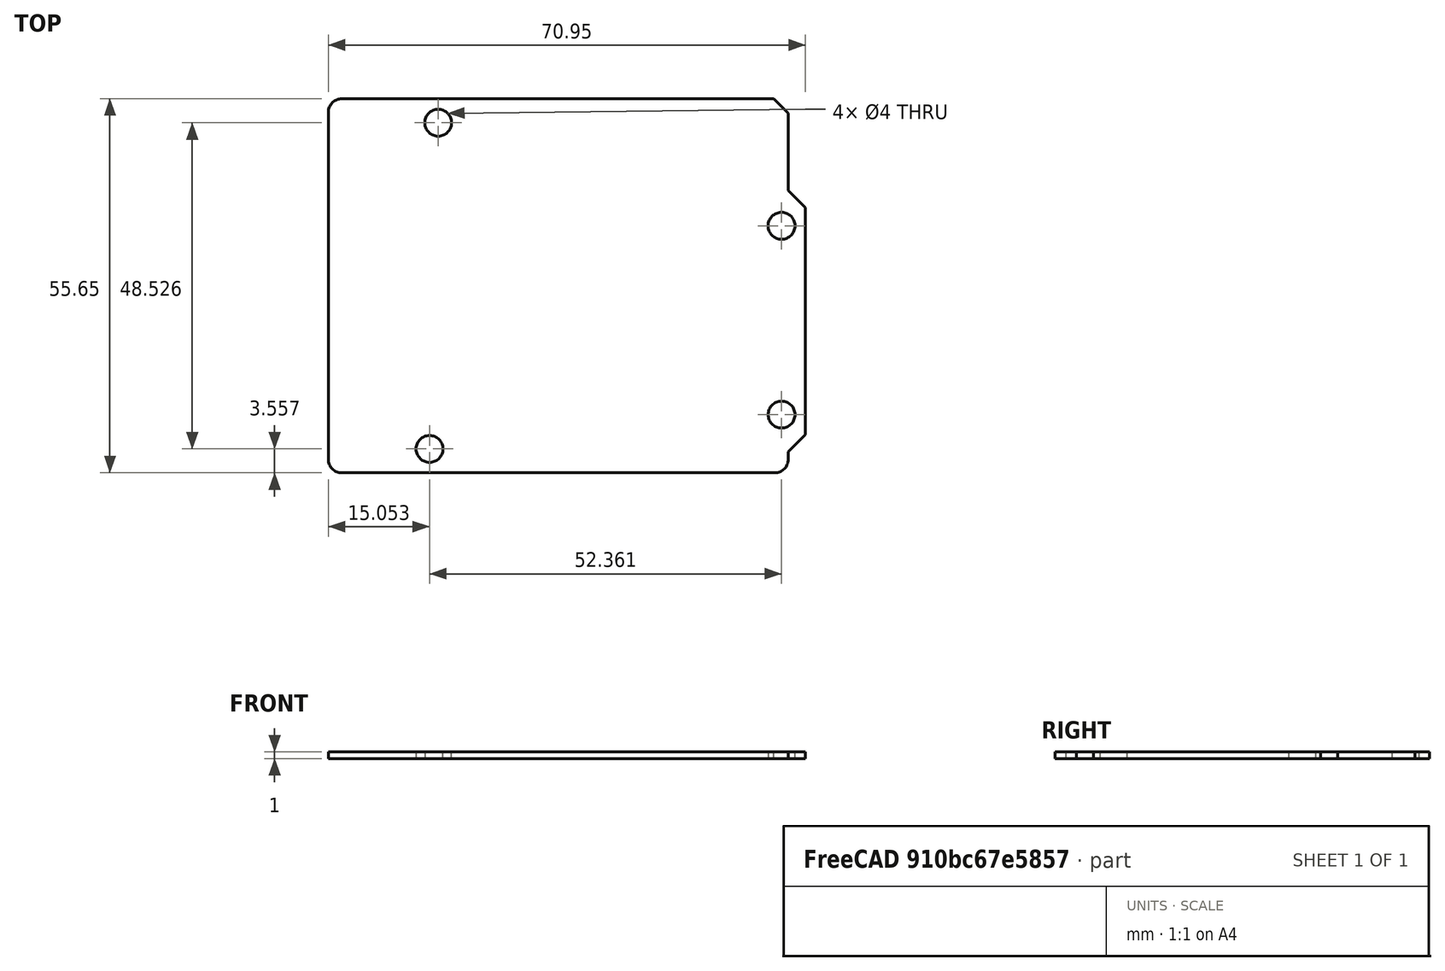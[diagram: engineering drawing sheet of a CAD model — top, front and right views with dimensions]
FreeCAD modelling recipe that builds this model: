
FCSTD DOCUMENT  (FreeCAD 0.19R)
Label: CAIXA-ARDUINO_01
License: Creative Commons Attribution-NonCommercial-ShareAlike
LicenseURL: http://creativecommons.org/licenses/by-nc-sa/4.0/
objects: Part::Feature×1, Sketcher::SketchObject×1, Part::Extrusion×1
note: 3 computed .brp shape members not serialized (recipe doc carries the construction recipe); baked Part::Feature solids carry a one-line shape summary decoded from their .brp

FEATURE [Part::Feature] ARDUINO_3D_SCALED
  Placement = pos=(-1,-1,0) rot=(0,0,1;0rad)
  shape: bbox 75.35 x 53.65 x 13.2 mm, 104 faces, 0 solids (baked)
FEATURE [Sketcher::SketchObject] Sketch
  ExternalGeometry = -> [ARDUINO_3D_SCALED]
  sketch-geometry (25):
    g0: LineSegment StartX=1 StartY=54.65 StartZ=0 EndX=65.2642 EndY=54.65 EndZ=0
    g1: LineSegment StartX=65.2642 StartY=54.65 StartZ=0 EndX=67.4 EndY=52.5142 EndZ=0
    g2: LineSegment StartX=67.4 StartY=52.5142 StartZ=0 EndX=67.4 EndY=41.0142 EndZ=0
    g3: LineSegment StartX=67.4 StartY=41.0142 StartZ=0 EndX=69.95 EndY=38.4642 EndZ=0
    g4: LineSegment StartX=69.95 StartY=38.4642 StartZ=0 EndX=69.95 EndY=4.68579 EndZ=0
    g5: LineSegment StartX=69.95 StartY=4.68579 StartZ=0 EndX=67.4 EndY=2.13579 EndZ=0
    g6: LineSegment StartX=67.4 StartY=2.13579 StartZ=0 EndX=67.4 EndY=1 EndZ=0
    g7: LineSegment StartX=65.4 StartY=-1 StartZ=0 EndX=1 EndY=-1 EndZ=0
    g8: LineSegment StartX=-1 StartY=1 StartZ=0 EndX=-1 EndY=52.65 EndZ=0
    g9: ArcOfCircle CenterX=1 CenterY=52.65 CenterZ=0 NormalX=0 NormalY=0 NormalZ=1 AngleXU=0 Radius=2 StartAngle=1.5708 EndAngle=3.14159
    g10: ArcOfCircle CenterX=1 CenterY=1 CenterZ=0 NormalX=0 NormalY=0 NormalZ=1 AngleXU=0 Radius=2 StartAngle=3.14159 EndAngle=4.71239
    g11: ArcOfCircle CenterX=65.4 CenterY=1 CenterZ=0 NormalX=0 NormalY=0 NormalZ=1 AngleXU=0 Radius=2 StartAngle=4.71239 EndAngle=6.28319
    g12: LineSegment [constr] StartX=67.675 StartY=39.325 StartZ=0 EndX=68.3821 EndY=40.0321 EndZ=0
    g13: LineSegment [constr] StartX=66.4 StartY=46.35 StartZ=0 EndX=67.4 EndY=46.35 EndZ=0
    g14: LineSegment [constr] StartX=65.625 StartY=52.875 StartZ=0 EndX=66.3321 EndY=53.5821 EndZ=0
    g15: LineSegment [constr] StartX=32.925 StartY=53.65 StartZ=0 EndX=32.925 EndY=54.65 EndZ=0
    g16: LineSegment [constr] StartX=4e-16 StartY=26.825 StartZ=0 EndX=-1 EndY=26.825 EndZ=0
    g17: LineSegment [constr] StartX=39.1673 StartY=1e-16 StartZ=0 EndX=39.1673 EndY=-1 EndZ=0
    g18: LineSegment [constr] StartX=66.4 StartY=1.56789 StartZ=0 EndX=67.4 EndY=1.56789 EndZ=0
    g19: LineSegment [constr] StartX=67.675 StartY=3.825 StartZ=0 EndX=68.3821 EndY=3.11789 EndZ=0
    g20: LineSegment [constr] StartX=68.95 StartY=21.575 StartZ=0 EndX=69.95 EndY=21.575 EndZ=0
    g21: Circle CenterX=15.3341 CenterY=51.0829 CenterZ=0 NormalX=0 NormalY=0 NormalZ=1 AngleXU=0 Radius=2
    g22: Circle CenterX=66.41 CenterY=35.7498 CenterZ=0 NormalX=0 NormalY=0 NormalZ=1 AngleXU=0 Radius=2
    g23: Circle CenterX=66.4139 CenterY=7.6684 CenterZ=0 NormalX=0 NormalY=0 NormalZ=1 AngleXU=0 Radius=2
    g24: Circle CenterX=14.0525 CenterY=2.55698 CenterZ=0 NormalX=0 NormalY=0 NormalZ=1 AngleXU=0 Radius=2
  constraints (65):
    c: Horizontal(g0)
    c: Coincident(g0,g1)
    c: Coincident(g1,g2)
    c: Vertical(g2)
    c: Coincident(g2,g3)
    c: Coincident(g3,g4)
    c: Coincident(g4,g5)
    c: Coincident(g5,g6)
    c: Vertical(g6)
    c: Horizontal(g7)
    c: Vertical(g8)
    c: Vertical(g4)
    c: Tangent(g0,g9) = 1.5708
    c: Tangent(g8,g9) = 1.5708
    c: Tangent(g7,g10) = 1.5708
    c: Tangent(g8,g10) = 1.5708
    c: Tangent(g6,g11) = 1.5708
    c: Tangent(g7,g11) = 1.5708
    c: Coincident(g11,g-6)
    c: Coincident(g10,g-4)
    c: Coincident(g9,g-14)
    c: Parallel(g3,g-10)
    c: Parallel(g-12,g1)
    c: Parallel(g5,g-8)
    c: PointOnObject(g12,g3)
    c: PointOnObject(g13,g2)
    c: Horizontal(g13)
    c: PointOnObject(g14,g1)
    c: Vertical(g15)
    c: PointOnObject(g16,g8)
    c: PointOnObject(g17,g-3)
    c: PointOnObject(g17,g7)
    c: Horizontal(g18)
    c: PointOnObject(g19,g5)
    c: PointOnObject(g20,g4)
    c: Horizontal(g20)
    c: Symmetric(g-9,g-9,g20)
    c: Symmetric(g-10,g-10,g12)
    c: Symmetric(g-11,g-11,g13)
    c: Perpendicular(g12,g-10)
    c: Symmetric(g-12,g-12,g14)
    c: Perpendicular(g-12,g14)
    c: Symmetric(g-13,g-13,g15)
    c: Symmetric(g-5,g-5,g16)
    c: Horizontal(g16)
    c: Symmetric(g-8,g-8,g19)
    c: Perpendicular(g-8,g19)
    c: Equal(g20,g12)
    c: Equal(g12,g13)
    c: Equal(g13,g14)
    c: Equal(g14,g15)
    c: Equal(g15,g16)
    c: Equal(g16,g17)
    c: Equal(g17,g18)
    c: Equal(g18,g19)
    c: Symmetric(g6,g6,g18)
    c: DistanceY(g15,g15) = 1
    c: Coincident(g21,g-18)
    c: Coincident(g22,g-17)
    c: Coincident(g23,g-16)
    c: Coincident(g24,g-15)
    c: Equal(g24,g23)
    c: Equal(g23,g22)
    c: Equal(g22,g21)
    c: Diameter(g21) = 4
FEATURE [Part::Extrusion] Extrude
  Base = -> Sketch
  Dir = (0,0,1)
  DirMode = 2
  FaceMakerClass = Part::FaceMakerBullseye
  LengthFwd = 1
  LengthRev = 0
  Solid = true
  Symmetric = false
